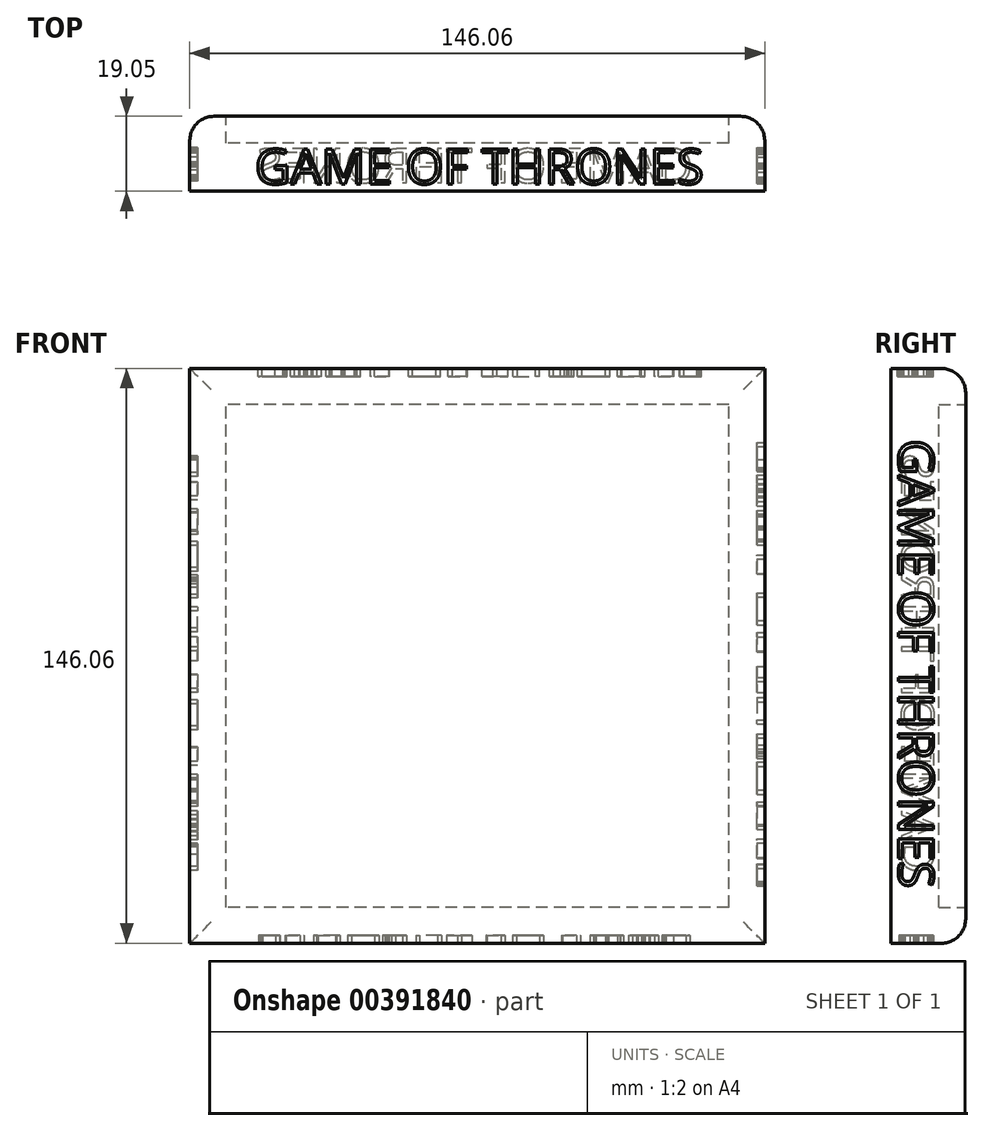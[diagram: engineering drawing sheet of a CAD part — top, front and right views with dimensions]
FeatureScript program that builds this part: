
annotation { "Feature Type Name" : "Feature", "Feature Type Description" : "" }
export const myFeature = defineFeature(function(context is Context, id is Id, definition is map)
    precondition{}
    {
        {
            var Q0;
            Q0=qCreatedBy(makeId("Front.planeOp"),FACE);
            var sketch = newSketch(context, id + "F0", { "sketchPlane" : qUnion([Q0])});
            skLineSegment(sketch, "E0.bottom", {"start": v(63.88, -63.88) * mm, "end": v(-63.88, -63.88) * mm});
            skLineSegment(sketch, "E0.top", {"start": v(63.88, 63.88) * mm, "end": v(-63.88, 63.88) * mm});
            skLineSegment(sketch, "E0.left", {"start": v(63.88, -63.88) * mm, "end": v(63.88, 63.88) * mm});
            skLineSegment(sketch, "E0.right", {"start": v(-63.88, -63.88) * mm, "end": v(-63.88, 63.88) * mm});
            skPoint(sketch, "E0.middle", {"position": v(0, 0) * mm});
            skSolve(sketch);
        }
        {
            var Q0;
            Q0=qCreatedBy(makeId("Front.planeOp"),FACE);
            var sketch = newSketch(context, id + "F1", { "sketchPlane" : qUnion([Q0])});
            skLineSegment(sketch, "E1.bottom", {"start": v(73.03, -73.02) * mm, "end": v(-73.03, -73.03) * mm});
            skLineSegment(sketch, "E1.top", {"start": v(73.03, 73.03) * mm, "end": v(-73.03, 73.02) * mm});
            skLineSegment(sketch, "E1.left", {"start": v(73.03, -73.02) * mm, "end": v(73.03, 73.03) * mm});
            skLineSegment(sketch, "E1.right", {"start": v(-73.03, -73.03) * mm, "end": v(-73.03, 73.02) * mm});
            skPoint(sketch, "E1.middle", {"position": v(0, 0) * mm});
            skSolve(sketch);
        }
        {
            var Q0;
            Q0=makeQuery(id+"F1.imprint","IMPRINT",FACE,{"disambiguationData":[TD([[makeQuery(id+"F1.imprint","IMPRINT",EDGE,{"derivedFrom":sQuery(id+"F1.wireOp",EDGE,"E1.bottom")}),-1.0]])]});
            extrude(context, id + "F2", {"entities" : qUnion([Q0]), "depth" : 19.05 * mm});
        }
        {
            var Q0;
            Q0 = qSketchRegion(id + "F0", true);
            extrude(context, id + "F3", {"entities" : qUnion([Q0]), "operationType" : NewBodyOperationType.REMOVE, "depth" : 6.86 * mm});
        }
        {
            var Q0;
            Q0=makeQuery(id+"F2.opExtrude","CAP_EDGE",EDGE,{"disambiguationData":[OSD([sQuery(id+"F1.wireOp",EDGE,"E1.left")])],"isStart":true});
            var Q1;
            Q1=makeQuery(id+"F2.opExtrude","CAP_EDGE",EDGE,{"disambiguationData":[OSD([sQuery(id+"F1.wireOp",EDGE,"E1.bottom")])],"isStart":true});
            var Q2;
            Q2=makeQuery(id+"F2.opExtrude","CAP_EDGE",EDGE,{"disambiguationData":[OSD([sQuery(id+"F1.wireOp",EDGE,"E1.right")])],"isStart":true});
            var Q3;
            Q3=makeQuery(id+"F2.opExtrude","CAP_EDGE",EDGE,{"disambiguationData":[OSD([sQuery(id+"F1.wireOp",EDGE,"E1.top")])],"isStart":true});
            fillet(context, id + "F4", {"entities" : qUnion([Q0, Q1, Q2, Q3]), "radius" : 6.13 * mm, "tangentPropagation" : true, "allowEdgeOverflow" : false});
        }
        {
            var Q0;
            Q0=makeQuery(id+"F2.opExtrude","SWEPT_FACE",FACE,{"disambiguationData":[OSD([sQuery(id+"F1.wireOp",EDGE,"E1.top")])]});
            var sketch = newSketch(context, id + "F5", { "sketchPlane" : qUnion([Q0])});
            skText(sketch, "E2", { "text": "GAME OF THRONES", "fontName": "OpenSans-Regular.ttf"});
            const initialGuessF5  = {"E2": [-0.0565, -0.01722, 1, 0, 0.00894]};
            skSetInitialGuess(sketch, initialGuessF5);
            skSolve(sketch);
        }
        {
            var Q0;
            Q0 = qSketchRegion(id + "F5", true);
            extrude(context, id + "F6", {"entities" : qUnion([Q0]), "operationType" : NewBodyOperationType.REMOVE, "oppositeDirection" : true, "depth" : 2.03 * mm});
        }
        {
            var Q0;
            Q0=makeQuery(id+"F2.opExtrude","SWEPT_FACE",FACE,{"disambiguationData":[OSD([sQuery(id+"F1.wireOp",EDGE,"E1.left")])]});
            var sketch = newSketch(context, id + "F7", { "sketchPlane" : qUnion([Q0])});
            skText(sketch, "E3", { "text": "GAME OF THRONES", "fontName": "OpenSans-Regular.ttf"});
            const initialGuessF7  = {"E3": [-0.01702, 0.055, 0, -1, 0.00894]};
            skSetInitialGuess(sketch, initialGuessF7);
            skSolve(sketch);
        }
        {
            var Q0;
            Q0 = qSketchRegion(id + "F7", true);
            extrude(context, id + "F8", {"entities" : qUnion([Q0]), "operationType" : NewBodyOperationType.REMOVE, "oppositeDirection" : true, "depth" : 2.03 * mm});
        }
        {
            var Q0;
            Q0=makeQuery(id+"F2.opExtrude","SWEPT_FACE",FACE,{"disambiguationData":[OSD([sQuery(id+"F1.wireOp",EDGE,"E1.bottom")])]});
            var sketch = newSketch(context, id + "F9", { "sketchPlane" : qUnion([Q0])});
            skText(sketch, "E4", { "text": "GAME OF THRONES", "fontName": "OpenSans-Regular.ttf"});
            const initialGuessF9  = {"E4": [0.0548, 0.0169, -1, 0, 0.0087]};
            skSetInitialGuess(sketch, initialGuessF9);
            skSolve(sketch);
        }
        {
            var Q0;
            Q0 = qSketchRegion(id + "F9", true);
            extrude(context, id + "F10", {"entities" : qUnion([Q0]), "operationType" : NewBodyOperationType.REMOVE, "oppositeDirection" : true, "depth" : 2.03 * mm});
        }
        {
            var Q0;
            Q0=makeQuery(id+"F2.opExtrude","SWEPT_FACE",FACE,{"disambiguationData":[OSD([sQuery(id+"F1.wireOp",EDGE,"E1.right")])]});
            var sketch = newSketch(context, id + "F11", { "sketchPlane" : qUnion([Q0])});
            skText(sketch, "E5", { "text": "GAME OF THRONES", "fontName": "OpenSans-Regular.ttf"});
            const initialGuessF11  = {"E5": [0.01634, -0.0552, 0, 1, 0.00835]};
            skSetInitialGuess(sketch, initialGuessF11);
            skSolve(sketch);
        }
        {
            var Q0;
            Q0 = qSketchRegion(id + "F11", true);
            extrude(context, id + "F12", {"entities" : qUnion([Q0]), "operationType" : NewBodyOperationType.REMOVE, "oppositeDirection" : true, "depth" : 2.03 * mm});
        }
    });
